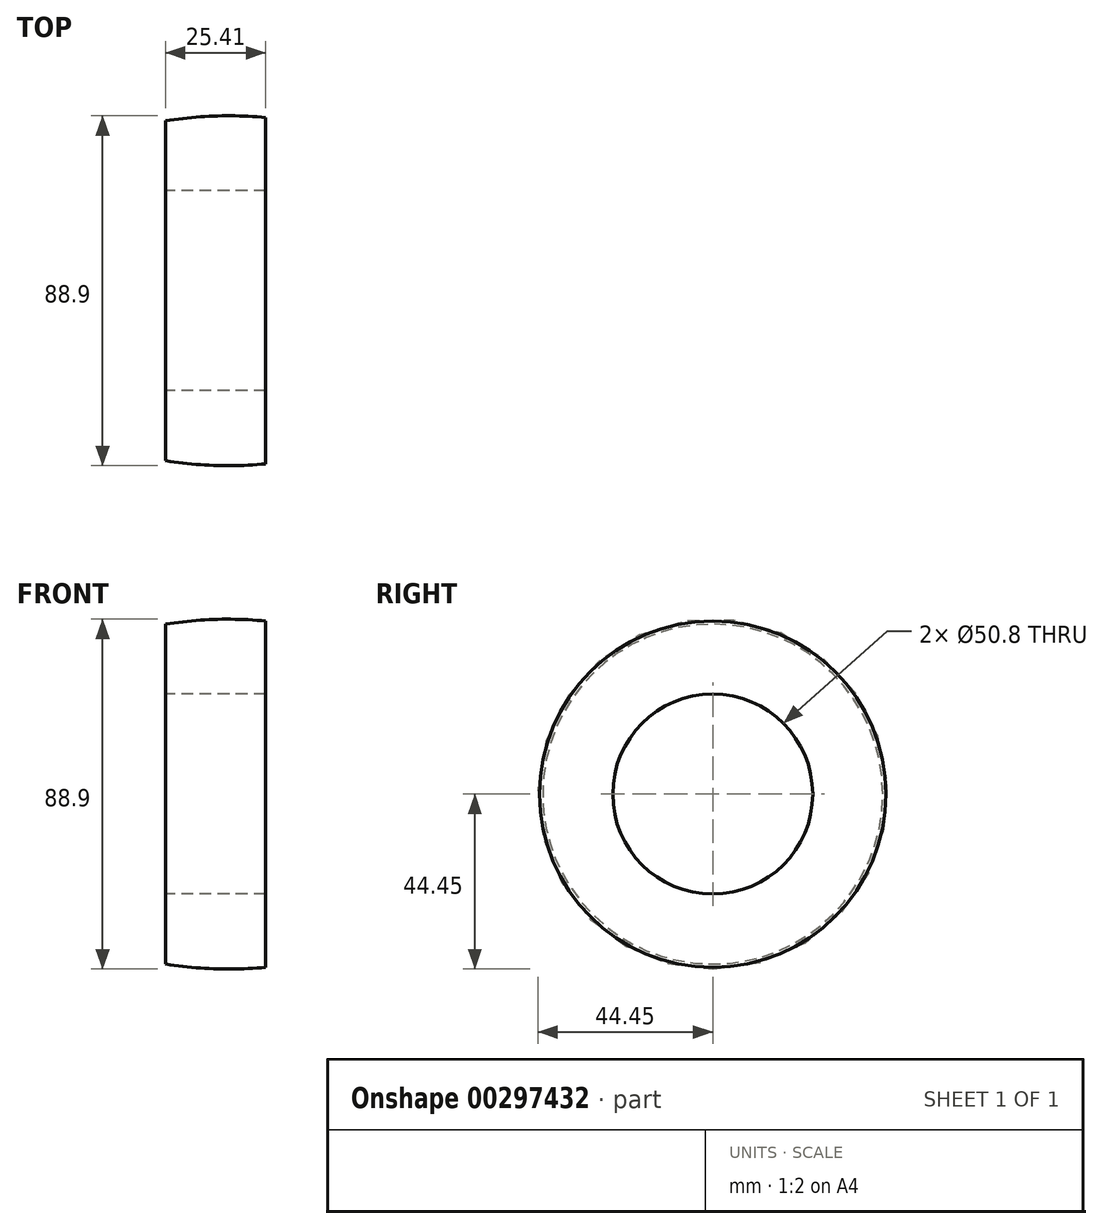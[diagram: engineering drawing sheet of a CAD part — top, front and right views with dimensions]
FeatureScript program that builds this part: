
annotation { "Feature Type Name" : "Feature", "Feature Type Description" : "" }
export const myFeature = defineFeature(function(context is Context, id is Id, definition is map)
    precondition{}
    {
        {
            var Q0;
            Q0=qCreatedBy(makeId("Front.planeOp"),FACE);
            var sketch = newSketch(context, id + "F0", { "sketchPlane" : qUnion([Q0])});
            skLineSegment(sketch, "E0", {"start": v(0, 0) * mm, "end": v(-38.14, 0) * mm, "construction": true});
            skLineSegment(sketch, "E1", {"start": v(0, 0) * mm, "end": v(0, 45.32) * mm, "construction": true});
            skLineSegment(sketch, "E2", {"start": v(0, 6.35) * mm, "end": v(-17.46, 6.35) * mm});
            skLineSegment(sketch, "E3", {"start": v(-17.46, 6.35) * mm, "end": v(-17.46, 15.88) * mm});
            skLineSegment(sketch, "E4", {"start": v(-17.46, 15.88) * mm, "end": v(-15.88, 15.88) * mm});
            skLineSegment(sketch, "E5", {"start": v(-15.87, 18.41) * mm, "end": v(-15.87, 43.18) * mm});
            skArc(sketch, "E6", {"start": v(-15.88, 15.88) * mm, "mid": v(-14.6, 17.14) * mm, "end": v(-15.88, 18.41) * mm});
            skArc(sketch, "E7", {"start": v(0, 44.45) * mm, "mid": v(-7.96, 44.13) * mm, "end": v(-15.87, 43.18) * mm});
            skLineSegment(sketch, "E8", {"start": v(0, 44.45) * mm, "end": v(13.35, 44.45) * mm, "construction": true});
            skLineSegment(sketch, "E9.MirrorCS", {"start": v(17.46, 15.88) * mm, "end": v(15.88, 15.88) * mm});
            skLineSegment(sketch, "E10.MirrorCS", {"start": v(17.46, 6.35) * mm, "end": v(17.46, 15.88) * mm});
            skArc(sketch, "E11.MirrorCS", {"start": v(0, 44.45) * mm, "mid": v(7.96, 44.13) * mm, "end": v(15.88, 43.18) * mm});
            skLineSegment(sketch, "E12.MirrorCS", {"start": v(15.88, 18.41) * mm, "end": v(15.88, 43.18) * mm});
            skLineSegment(sketch, "E13.MirrorCS", {"start": v(0, 6.35) * mm, "end": v(17.46, 6.35) * mm});
            skArc(sketch, "E14.MirrorCS", {"start": v(15.88, 15.88) * mm, "mid": v(14.6, 17.14) * mm, "end": v(15.88, 18.41) * mm});
            skSolve(sketch);
        }
        {
            var Q0;
            Q0 = qSketchRegion(id + "F0", true);
            var Q1;
            Q1=sQuery(id+"F0.wireOp",EDGE,"E0");
            revolve(context, id + "F1", {"entities" : qUnion([Q0]), "axis" : qUnion([Q1]), "revolveType" : RevolveType.FULL});
        }
        {
            var Q0;
            Q0=makeQuery(id+"F1.opRevolve","SWEPT_BODY",BODY,{"disambiguationData":[OSD([sQuery(id+"F0.wireOp",EDGE,"E2"),sQuery(id+"F0.wireOp",EDGE,"E3"),sQuery(id+"F0.wireOp",EDGE,"E4"),sQuery(id+"F0.wireOp",EDGE,"E5"),sQuery(id+"F0.wireOp",EDGE,"E6"),sQuery(id+"F0.wireOp",EDGE,"E7"),sQuery(id+"F0.wireOp",EDGE,"E9.MirrorCS"),sQuery(id+"F0.wireOp",EDGE,"E10.MirrorCS"),sQuery(id+"F0.wireOp",EDGE,"E11.MirrorCS"),sQuery(id+"F0.wireOp",EDGE,"E12.MirrorCS"),sQuery(id+"F0.wireOp",EDGE,"E13.MirrorCS"),sQuery(id+"F0.wireOp",EDGE,"E14.MirrorCS")])]});
            transform(context, id + "F2", {"entities" : qUnion([Q0]), "transformType" : TransformType.COPY});
        }
        {
            var Q0;
            Q0=qCreatedBy(makeId("Right.planeOp"),FACE);
            var sketch = newSketch(context, id + "F3", { "sketchPlane" : qUnion([Q0])});
            skCircle(sketch, "E15", {"center": v(0, 0) * mm, "radius": 25.4 * mm});
            skSolve(sketch);
        }
        {
            var Q0;
            Q0 = qSketchRegion(id + "F3", true);
            extrude(context, id + "F4", {"entities" : qUnion([Q0]), "operationType" : NewBodyOperationType.REMOVE, "endBound" : BoundingType.SYMMETRIC, "depth" : 50.8 * mm});
        }
        {
            var Q0;
            Q0=qCreatedBy(makeId("Right.planeOp"),FACE);
            var sketch = newSketch(context, id + "F5", { "sketchPlane" : qUnion([Q0])});
            skCircle(sketch, "E16", {"center": v(0, 0) * mm, "radius": 15.88 * mm});
            skSolve(sketch);
        }
        {
            var Q0;
            Q0 = qSketchRegion(id + "F5", true);
            extrude(context, id + "F6", {"entities" : qUnion([Q0]), "operationType" : NewBodyOperationType.REMOVE, "endBound" : BoundingType.SYMMETRIC, "oppositeDirection" : true, "depth" : 50.8 * mm});
        }
        {
            var Q0;
            Q0=makeQuery(id+"F2.opPattern","COPY",FACE,{"derivedFrom":makeQuery(id+"F1.opRevolve","SWEPT_FACE",FACE,{"disambiguationData":[OSD([sQuery(id+"F0.wireOp",EDGE,"E12.MirrorCS")])]}),"instanceName":"1"});
            var sketch = newSketch(context, id + "F7", { "sketchPlane" : qUnion([Q0])});
            skCircle(sketch, "E17", {"center": v(0, 0) * mm, "radius": 50.4 * mm});
            skSolve(sketch);
        }
        {
            var Q0;
            Q0 = qSketchRegion(id + "F7", true);
            extrude(context, id + "F8", {"entities" : qUnion([Q0]), "operationType" : NewBodyOperationType.REMOVE, "oppositeDirection" : true, "depth" : 6.35 * mm});
        }
    });
